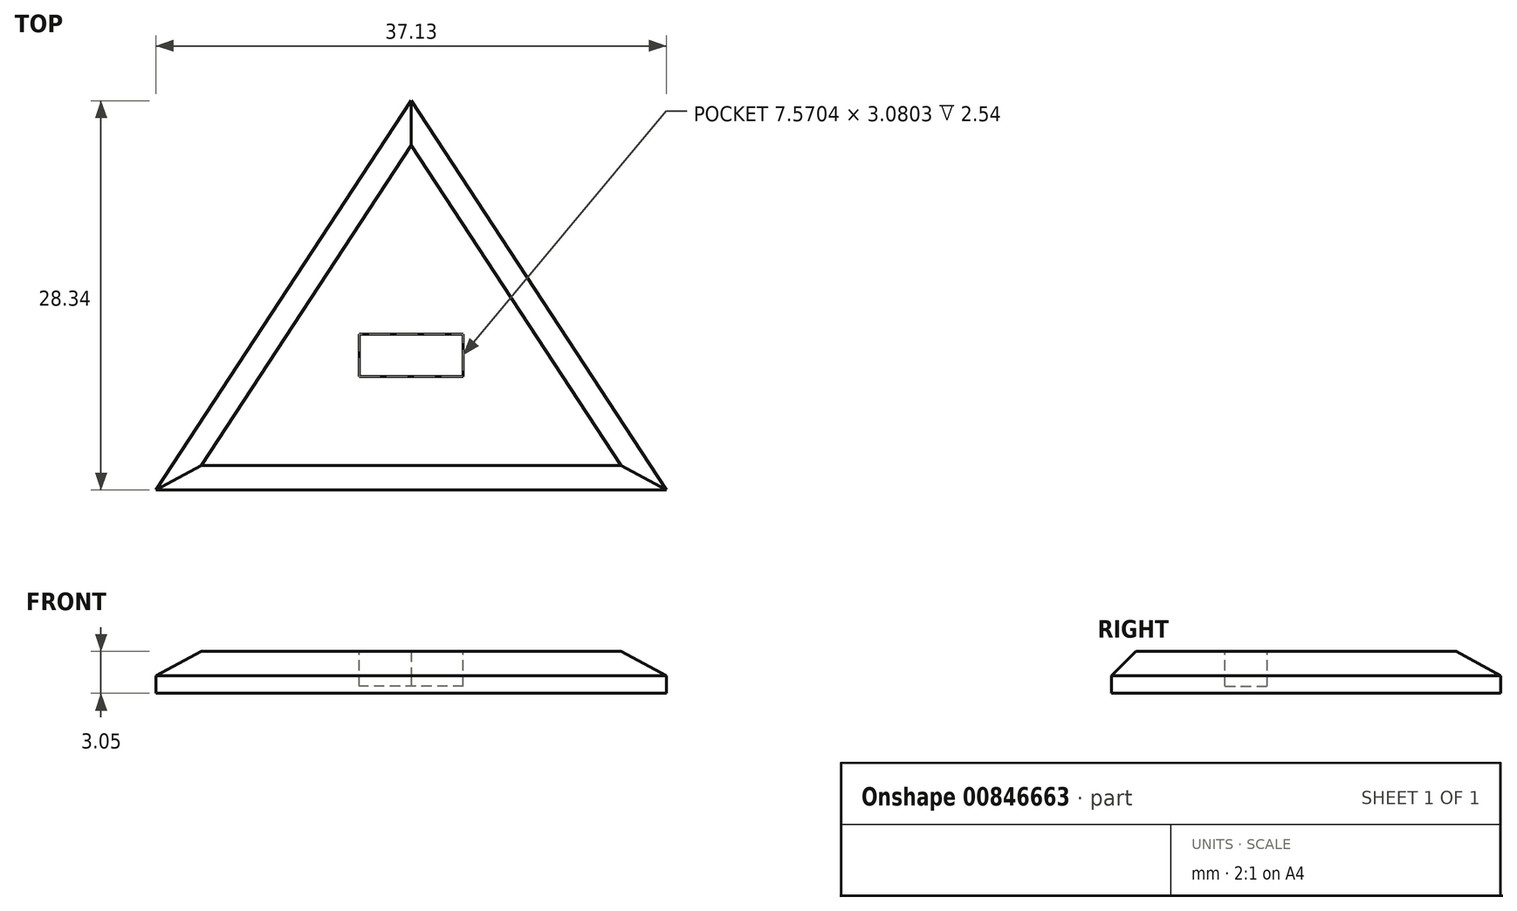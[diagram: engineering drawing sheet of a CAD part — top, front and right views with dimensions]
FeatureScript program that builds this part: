
annotation { "Feature Type Name" : "Feature", "Feature Type Description" : "" }
export const myFeature = defineFeature(function(context is Context, id is Id, definition is map)
    precondition{}
    {
        {
            var Q0;
            Q0=qCreatedBy(makeId("Top.planeOp"),FACE);
            var sketch = newSketch(context, id + "F0", { "sketchPlane" : qUnion([Q0])});
            skLineSegment(sketch, "E0", {"start": v(0, 0) * mm, "end": v(0, 28.34) * mm, "construction": true});
            skLineSegment(sketch, "E1", {"start": v(0, 28.34) * mm, "end": v(0, -27.2) * mm, "construction": true});
            skLineSegment(sketch, "E2", {"start": v(0, 0) * mm, "end": v(18.56, 0) * mm});
            skLineSegment(sketch, "E3", {"start": v(18.56, 0) * mm, "end": v(0, 28.34) * mm});
            skLineSegment(sketch, "E4", {"start": v(0, 28.34) * mm, "end": v(-18.57, 0) * mm});
            skLineSegment(sketch, "E5", {"start": v(-18.57, 0) * mm, "end": v(0, 0) * mm});
            skSolve(sketch);
        }
        {
            var Q0;
            Q0=makeQuery(id+"F0.imprint","IMPRINT",FACE,{"disambiguationData":[TD([[makeQuery(id+"F0.imprint","IMPRINT",EDGE,{"derivedFrom":sQuery(id+"F0.wireOp",EDGE,"E2")}),1.0]])]});
            extrude(context, id + "F1", {"entities" : qUnion([Q0]), "depth" : 3.05 * mm, "offsetDistance" : 25.4 * mm});
        }
        {
            var Q0;
            Q0=makeQuery(id+"F1.opExtrude","CAP_EDGE",EDGE,{"disambiguationData":[OSD([sQuery(id+"F0.wireOp",EDGE,"E4")])],"isStart":false});
            var Q1;
            Q1=makeQuery(id+"F1.opExtrude","CAP_EDGE",EDGE,{"disambiguationData":[OSD([sQuery(id+"F0.wireOp",EDGE,"E2"),sQuery(id+"F0.wireOp",EDGE,"E5")])],"isStart":false});
            var Q2;
            Q2=makeQuery(id+"F1.opExtrude","CAP_EDGE",EDGE,{"disambiguationData":[OSD([sQuery(id+"F0.wireOp",EDGE,"E3")])],"isStart":false});
            chamfer(context, id + "F2", {"entities" : qUnion([Q0, Q1, Q2]), "width" : 1.78 * mm, "tangentPropagation" : true});
        }
        {
            var Q0;
            Q0=makeQuery(id+"F1.opExtrude","CAP_FACE",FACE,{"disambiguationData":[OSD([sQuery(id+"F0.wireOp",EDGE,"E2"),sQuery(id+"F0.wireOp",EDGE,"E3"),sQuery(id+"F0.wireOp",EDGE,"E4"),sQuery(id+"F0.wireOp",EDGE,"E5")])],"isStart":false});
            var sketch = newSketch(context, id + "F3", { "sketchPlane" : qUnion([Q0])});
            skLineSegment(sketch, "E6.bottom", {"start": v(3.79, 8.27) * mm, "end": v(-3.79, 8.27) * mm});
            skLineSegment(sketch, "E6.top", {"start": v(3.79, 11.35) * mm, "end": v(-3.79, 11.35) * mm});
            skLineSegment(sketch, "E6.left", {"start": v(3.79, 8.27) * mm, "end": v(3.79, 11.35) * mm});
            skLineSegment(sketch, "E6.right", {"start": v(-3.79, 8.27) * mm, "end": v(-3.79, 11.35) * mm});
            skPoint(sketch, "E6.middle", {"position": v(0, 9.81) * mm});
            skSolve(sketch);
        }
        {
            var Q0;
            Q0=makeQuery(id+"F3.imprint","IMPRINT",FACE,{"disambiguationData":[TD([[makeQuery(id+"F3.imprint","IMPRINT",EDGE,{"derivedFrom":sQuery(id+"F3.wireOp",EDGE,"E6.bottom")}),-1.0]])]});
            extrude(context, id + "F4", {"entities" : qUnion([Q0]), "operationType" : NewBodyOperationType.REMOVE, "oppositeDirection" : true, "depth" : 0.5 * mm, "offsetDistance" : 25.4 * mm});
        }
        {
            var Q0;
            Q0=makeQuery(id+"F4.boolean.opBoolean","COPY",FACE,{"derivedFrom":makeQuery(id+"F4.opExtrude","CAP_FACE",FACE,{"disambiguationData":[OSD([sQuery(id+"F3.wireOp",EDGE,"E6.bottom"),sQuery(id+"F3.wireOp",EDGE,"E6.top"),sQuery(id+"F3.wireOp",EDGE,"E6.left"),sQuery(id+"F3.wireOp",EDGE,"E6.right")])],"isStart":false})});
            extrude(context, id + "F5", {"entities" : qUnion([Q0]), "operationType" : NewBodyOperationType.REMOVE, "oppositeDirection" : true, "depth" : 2.03 * mm, "offsetDistance" : 25.4 * mm});
        }
    });
